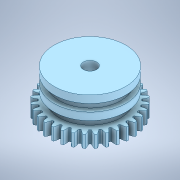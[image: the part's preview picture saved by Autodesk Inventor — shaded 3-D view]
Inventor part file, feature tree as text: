
AUTODESK INVENTOR PART (.ipt)
format: ipt  version: 2022 (Build 260153000, 153)  size: 483,328 bytes
history: native  units: in
note: dims shown in document units (in); Inventor stores cm internally (conversion verified against a paired STEP export)
features: sketch x6, extrude x4, hole x2, other x1, plane x1
ambient origin geometry x8: Origin, YZ Plane, XZ Plane, XY Plane, X Axis, Y Axis, Z Axis, Center Point
bodies: Solid1 (feature_tree)
feature tree (14):
  other  "Part 1"
  extrude  "Extrusion1"  Depth=0.1181in TaperAngle=0.0deg
  extrude  "Extrusion2"  Depth=0.1181in TaperAngle=0.0deg
  extrude  "Extrusion3"  Depth=0.1181in TaperAngle=0.0deg
  extrude  "Extrusion4"  Depth=0.1181in TaperAngle=0.0deg
  hole  "Hole1"  [1 undecoded]
  plane  "Work Plane1"
  hole  "Hole2"  [1 undecoded]
  sketch  "Sketch1"  dims[d0=0.9843in d1=0.1181in d2=0.0in]
  sketch  "Sketch2"  dims[d3=1.1417in d4=0.1181in d5=0.0in]
  sketch  "Sketch4"  dims[d7=0.9843in d8=0.1181in d9=0.0in]
  sketch  "Sketch5"  dims[d10=1.1417in d11=0.1181in d12=0.0in]
  sketch  "Sketch6"  dims[d13=0.2126in d14=0.2362in d15=0.1575in d16=0.0787in d17=90.0deg d18=0.315in d19=0.8108in d20=0.0591in]
  sketch  "Sketch7"  dims[d21=0.0591in d22=0.0591in d23=0.2362in d24=0.1575in d25=0.0787in d26=90.0deg d27=0.315in d28=0.8108in]
note: 2 required parameter values undecoded (feature->parameter linkage not recoverable at this tier; creation-order binding heuristic only, values carry confidence <= 0.55)
